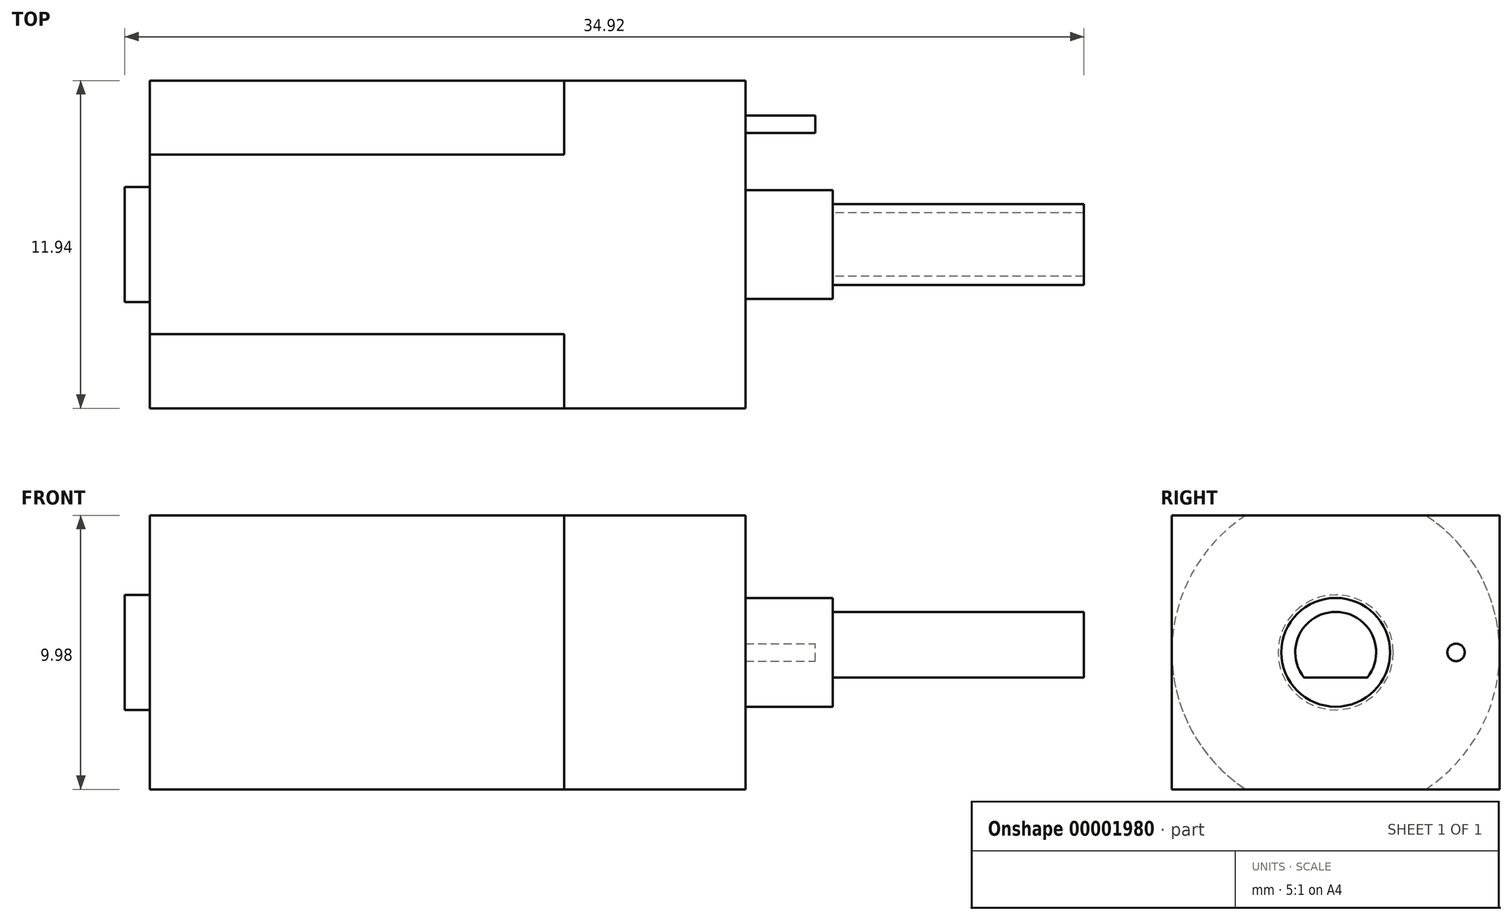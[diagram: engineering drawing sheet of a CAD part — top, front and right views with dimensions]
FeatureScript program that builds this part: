
annotation { "Feature Type Name" : "Feature", "Feature Type Description" : "" }
export const myFeature = defineFeature(function(context is Context, id is Id, definition is map)
    precondition{}
    {
        {
            var Q0;
            Q0=qCreatedBy(makeId("Right.planeOp"),FACE);
            var sketch = newSketch(context, id + "F0", { "sketchPlane" : qUnion([Q0])});
            skArc(sketch, "E0", {"start": v(-3.27, 5) * mm, "mid": v(-5.97, 0) * mm, "end": v(-3.27, -5) * mm});
            skCircle(sketch, "E1", {"center": v(0, 0) * mm, "radius": 5 * mm, "construction": true});
            skLineSegment(sketch, "E2", {"start": v(-3.27, 5) * mm, "end": v(3.27, 5) * mm});
            skLineSegment(sketch, "E3", {"start": v(3.27, -5) * mm, "end": v(-3.27, -5) * mm});
            skArc(sketch, "E4.trimOffspring", {"start": v(3.27, -5) * mm, "mid": v(5.97, 0) * mm, "end": v(3.27, 5) * mm});
            skCircle(sketch, "E5", {"center": v(0, 0) * mm, "radius": 2.1 * mm});
            skSolve(sketch);
        }
        {
            var Q0;
            Q0=makeQuery(id+"F0.imprint","IMPRINT",FACE,{"disambiguationData":[TD([[makeQuery(id+"F0.imprint","IMPRINT",EDGE,{"derivedFrom":sQuery(id+"F0.wireOp",EDGE,"E0")}),1.0]])]});
            var Q1;
            Q1=makeQuery(id+"F0.imprint","IMPRINT",FACE,{"disambiguationData":[TD([[makeQuery(id+"F0.imprint","IMPRINT",EDGE,{"derivedFrom":sQuery(id+"F0.wireOp",EDGE,"E5")}),1.0]])]});
            extrude(context, id + "F1", {"entities" : qUnion([Q0, Q1]), "depth" : 15.1 * mm});
        }
        {
            var Q0;
            Q0=makeQuery(id+"F1.opExtrude","CAP_FACE",FACE,{"disambiguationData":[OSD([sQuery(id+"F0.wireOp",EDGE,"E0"),sQuery(id+"F0.wireOp",EDGE,"E2"),sQuery(id+"F0.wireOp",EDGE,"E3"),sQuery(id+"F0.wireOp",EDGE,"E4.trimOffspring")])],"isStart":false});
            var sketch = newSketch(context, id + "F2", { "sketchPlane" : qUnion([Q0])});
            skLineSegment(sketch, "E6.bottom", {"start": v(-5.97, -5) * mm, "end": v(5.97, -5) * mm});
            skLineSegment(sketch, "E6.top", {"start": v(-5.97, 5) * mm, "end": v(5.97, 5) * mm});
            skLineSegment(sketch, "E6.left", {"start": v(-5.97, -5) * mm, "end": v(-5.97, 5) * mm});
            skLineSegment(sketch, "E6.right", {"start": v(5.97, -5) * mm, "end": v(5.97, 5) * mm});
            skSolve(sketch);
        }
        {
            var Q0;
            {var subQ0=makeQuery(id+"F1.opExtrude","CAP_EDGE",EDGE,{"disambiguationData":[OSD([sQuery(id+"F0.wireOp",EDGE,"E0")])],"isStart":false});var subQ3=sQuery(id+"F2.wireOp",EDGE,"E6.top");var subQ4=makeQuery(id+"F2.imprint","INTERSECT",VERTEX,{"derivedFrom":[subQ0,subQ3]});Q0=makeQuery(id+"F2.imprint","IMPRINT",FACE,{"disambiguationData":[TD([[makeQuery(id+"F2.imprint","IMPRINT",EDGE,{"disambiguationData":[TD([[subQ4,1.0]])],"derivedFrom":subQ3}),-1.0]])]});}
            var Q1;
            {var subQ0=makeQuery(id+"F1.opExtrude","CAP_EDGE",EDGE,{"disambiguationData":[OSD([sQuery(id+"F0.wireOp",EDGE,"E4.trimOffspring")])],"isStart":false});var subQ2=sQuery(id+"F2.wireOp",EDGE,"E6.bottom");var subQ3=makeQuery(id+"F2.imprint","INTERSECT",VERTEX,{"derivedFrom":[subQ0,subQ2]});var subQ6=makeQuery(id+"F1.opExtrude","CAP_EDGE",EDGE,{"disambiguationData":[OSD([sQuery(id+"F0.wireOp",EDGE,"E0")])],"isStart":false});var subQ8=makeQuery(id+"F2.imprint","INTERSECT",VERTEX,{"derivedFrom":[subQ6,subQ2]});Q1=makeQuery(id+"F2.imprint","IMPRINT",FACE,{"disambiguationData":[TD([[makeQuery(id+"F2.imprint","IMPRINT",EDGE,{"disambiguationData":[TD([[subQ8,1.0],[subQ3,-1.0]])],"derivedFrom":subQ2}),-1.0]])]});}
            var Q2;
            {var subQ0=makeQuery(id+"F1.opExtrude","CAP_EDGE",EDGE,{"disambiguationData":[OSD([sQuery(id+"F0.wireOp",EDGE,"E4.trimOffspring")])],"isStart":false});var subQ3=sQuery(id+"F2.wireOp",EDGE,"E6.top");var subQ4=makeQuery(id+"F2.imprint","INTERSECT",VERTEX,{"derivedFrom":[subQ0,subQ3]});Q2=makeQuery(id+"F2.imprint","IMPRINT",FACE,{"disambiguationData":[TD([[makeQuery(id+"F2.imprint","IMPRINT",EDGE,{"disambiguationData":[TD([[subQ4,-1.0]])],"derivedFrom":subQ3}),-1.0]])]});}
            var Q3;
            {var subQ0=makeQuery(id+"F1.opExtrude","CAP_EDGE",EDGE,{"disambiguationData":[OSD([sQuery(id+"F0.wireOp",EDGE,"E4.trimOffspring")])],"isStart":false});var subQ1=sQuery(id+"F2.wireOp",EDGE,"E6.right");var subQ3=sQuery(id+"F2.wireOp",EDGE,"E6.bottom");var subQ4=makeQuery(id+"F2.imprint","INTERSECT",VERTEX,{"derivedFrom":[subQ0,subQ3]});var subQ5=makeQuery(id+"F2.imprint","INTERSECT",VERTEX,{"derivedFrom":[subQ3,subQ1]});Q3=makeQuery(id+"F2.imprint","IMPRINT",FACE,{"disambiguationData":[TD([[makeQuery(id+"F2.imprint","IMPRINT",EDGE,{"disambiguationData":[TD([[subQ4,-1.0],[subQ5,1.0]])],"derivedFrom":subQ3}),1.0]])]});}
            var Q4;
            {var subQ0=makeQuery(id+"F1.opExtrude","CAP_EDGE",EDGE,{"disambiguationData":[OSD([sQuery(id+"F0.wireOp",EDGE,"E0")])],"isStart":false});var subQ1=sQuery(id+"F2.wireOp",EDGE,"E6.left");var subQ3=sQuery(id+"F2.wireOp",EDGE,"E6.bottom");var subQ4=makeQuery(id+"F2.imprint","INTERSECT",VERTEX,{"derivedFrom":[subQ0,subQ3]});var subQ5=makeQuery(id+"F2.imprint","INTERSECT",VERTEX,{"derivedFrom":[subQ3,subQ1]});Q4=makeQuery(id+"F2.imprint","IMPRINT",FACE,{"disambiguationData":[TD([[makeQuery(id+"F2.imprint","IMPRINT",EDGE,{"disambiguationData":[TD([[subQ4,1.0],[subQ5,-1.0]])],"derivedFrom":subQ3}),1.0]])]});}
            extrude(context, id + "F3", {"entities" : qUnion([Q0, Q1, Q2, Q3, Q4]), "operationType" : NewBodyOperationType.ADD, "depth" : 9.14 * mm});
        }
        {
            var Q0;
            Q0=makeQuery(id+"F3.opExtrude","CAP_FACE",FACE,{"disambiguationData":[OSD([sQuery(id+"F2.wireOp",EDGE,"E6.bottom"),sQuery(id+"F2.wireOp",EDGE,"E6.top"),sQuery(id+"F2.wireOp",EDGE,"E6.left"),sQuery(id+"F2.wireOp",EDGE,"E6.right")])],"isStart":false});
            var sketch = newSketch(context, id + "F4", { "sketchPlane" : qUnion([Q0])});
            skCircle(sketch, "E7", {"center": v(0, 0) * mm, "radius": 1.98 * mm});
            skCircle(sketch, "E8", {"center": v(0, 0.28) * mm, "radius": 1.2 * mm, "construction": true});
            skLineSegment(sketch, "E9", {"start": v(-1.16, -0.91) * mm, "end": v(1.16, -0.91) * mm});
            skArc(sketch, "E10", {"start": v(-1.16, -0.91) * mm, "mid": v(0, -1.47) * mm, "end": v(1.16, -0.91) * mm, "construction": true});
            skArc(sketch, "E11", {"start": v(1.16, -0.91) * mm, "mid": v(0, 1.47) * mm, "end": v(-1.16, -0.91) * mm});
            skCircle(sketch, "E12", {"center": v(-4.38, 0) * mm, "radius": 0.32 * mm});
            skCircle(sketch, "E13.0.MirrorC", {"center": v(4.38, 0) * mm, "radius": 0.32 * mm});
            skSolve(sketch);
        }
        {
            var Q0;
            Q0=makeQuery(id+"F4.imprint","IMPRINT",FACE,{"disambiguationData":[TD([[makeQuery(id+"F4.imprint","IMPRINT",EDGE,{"derivedFrom":sQuery(id+"F4.wireOp",EDGE,"E7")}),1.0]])]});
            extrude(context, id + "F5", {"entities" : qUnion([Q0]), "operationType" : NewBodyOperationType.ADD, "depth" : 0.64 * mm});
        }
        {
            var Q0;
            Q0=makeQuery(id+"F5.boolean.opBoolean","SPLIT",FACE,{"disambiguationData":[TD([makeQuery(id+"F5.opExtrude","SWEPT_FACE",FACE,{"disambiguationData":[OSD([sQuery(id+"F4.wireOp",EDGE,"E9")])]})])],"derivedFrom":makeQuery(id+"F3.opExtrude","CAP_FACE",FACE,{"disambiguationData":[OSD([sQuery(id+"F2.wireOp",EDGE,"E6.bottom"),sQuery(id+"F2.wireOp",EDGE,"E6.top"),sQuery(id+"F2.wireOp",EDGE,"E6.left"),sQuery(id+"F2.wireOp",EDGE,"E6.right")])],"isStart":false})});
            extrude(context, id + "F6", {"entities" : qUnion([Q0]), "operationType" : NewBodyOperationType.ADD, "depth" : 9.78 * mm});
        }
        {
            var Q0;
            Q0=makeQuery(id+"F0.imprint","IMPRINT",FACE,{"disambiguationData":[TD([[makeQuery(id+"F0.imprint","IMPRINT",EDGE,{"derivedFrom":sQuery(id+"F0.wireOp",EDGE,"E5")}),1.0]])]});
            extrude(context, id + "F7", {"entities" : qUnion([Q0]), "operationType" : NewBodyOperationType.ADD, "oppositeDirection" : true, "depth" : 0.91 * mm});
        }
        {
            var Q0;
            Q0=makeQuery(id+"F4.imprint","IMPRINT",FACE,{"disambiguationData":[TD([[makeQuery(id+"F4.imprint","IMPRINT",EDGE,{"derivedFrom":sQuery(id+"F4.wireOp",EDGE,"E12")}),1.0]])]});
            var Q1;
            Q1=makeQuery(id+"F4.imprint","IMPRINT",FACE,{"disambiguationData":[TD([[makeQuery(id+"F4.imprint","IMPRINT",EDGE,{"derivedFrom":sQuery(id+"F4.wireOp",EDGE,"E13.0.MirrorC")}),-1.0]])]});
            extrude(context, id + "F8", {"entities" : qUnion([Q0, Q1]), "operationType" : NewBodyOperationType.REMOVE, "oppositeDirection" : true, "depth" : 2.54 * mm});
        }
    });
